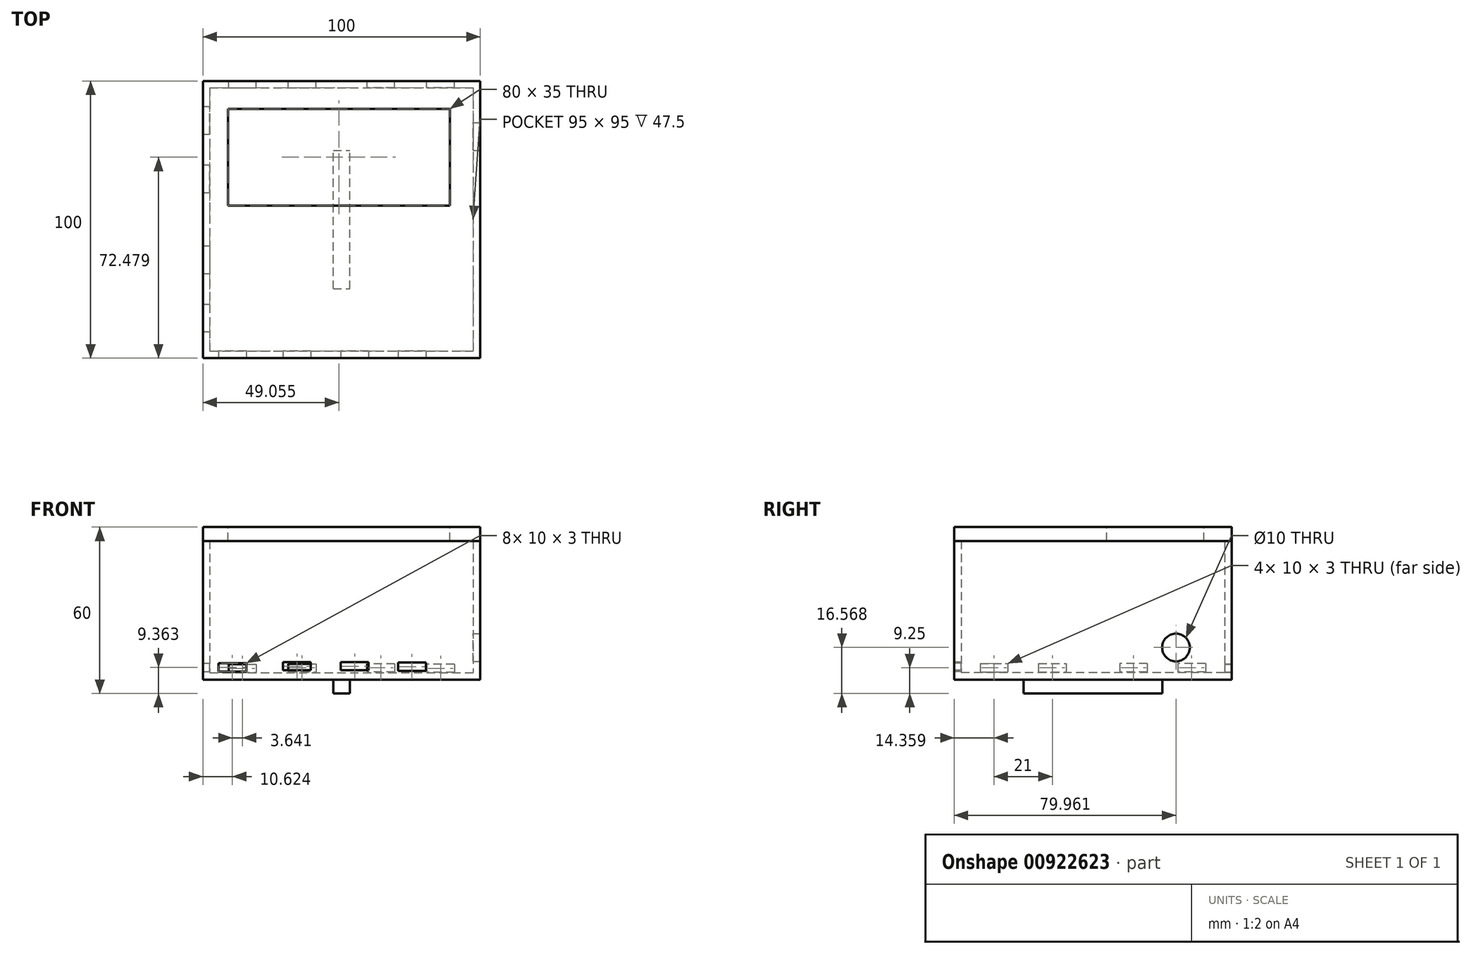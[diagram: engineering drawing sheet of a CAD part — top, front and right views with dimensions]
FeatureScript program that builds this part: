
annotation { "Feature Type Name" : "Feature", "Feature Type Description" : "" }
export const myFeature = defineFeature(function(context is Context, id is Id, definition is map)
    precondition{}
    {
        {
            var Q0;
            Q0=qCreatedBy(makeId("Top.planeOp"),FACE);
            var sketch = newSketch(context, id + "F0", { "sketchPlane" : qUnion([Q0])});
            skLineSegment(sketch, "E0.bottom", {"start": v(-50, 50) * mm, "end": v(50, 50) * mm});
            skLineSegment(sketch, "E0.top", {"start": v(-50, -50) * mm, "end": v(50, -50) * mm});
            skLineSegment(sketch, "E0.left", {"start": v(-50, 50) * mm, "end": v(-50, -50) * mm});
            skLineSegment(sketch, "E0.right", {"start": v(50, 50) * mm, "end": v(50, -50) * mm});
            skPoint(sketch, "E0.middle", {"position": v(0, 0) * mm});
            skSolve(sketch);
        }
        {
            var Q0;
            Q0=makeQuery(id+"F0.imprint","IMPRINT",FACE,{"disambiguationData":[TD([[makeQuery(id+"F0.imprint","IMPRINT",EDGE,{"derivedFrom":sQuery(id+"F0.wireOp",EDGE,"E0.bottom")}),-1.0]])]});
            extrude(context, id + "F1", {"entities" : qUnion([Q0]), "depth" : 50 * mm, "offsetDistance" : 25 * mm});
        }
        {
            var Q0;
            Q0=makeQuery(id+"F1.opExtrude","CAP_FACE",FACE,{"disambiguationData":[OSD([sQuery(id+"F0.wireOp",EDGE,"E0.bottom"),sQuery(id+"F0.wireOp",EDGE,"E0.top"),sQuery(id+"F0.wireOp",EDGE,"E0.left"),sQuery(id+"F0.wireOp",EDGE,"E0.right")])],"isStart":false});
            shell(context, id + "F2", {"entities" : qUnion([Q0]), "thickness" : 2.5 * mm});
        }
        {
            var Q0;
            Q0=makeQuery(id+"F1.opExtrude","SWEPT_FACE",FACE,{"disambiguationData":[OSD([sQuery(id+"F0.wireOp",EDGE,"E0.top")])]});
            var sketch = newSketch(context, id + "F3", { "sketchPlane" : qUnion([Q0])});
            skLineSegment(sketch, "E1.bottom", {"start": v(-44.38, 5.86) * mm, "end": v(-34.38, 5.86) * mm});
            skLineSegment(sketch, "E1.top", {"start": v(-44.38, 2.86) * mm, "end": v(-34.38, 2.86) * mm});
            skLineSegment(sketch, "E1.left", {"start": v(-44.38, 5.86) * mm, "end": v(-44.38, 2.86) * mm});
            skLineSegment(sketch, "E1.right", {"start": v(-34.38, 5.86) * mm, "end": v(-34.38, 2.86) * mm});
            skLineSegment(sketch, "E2.bottom", {"start": v(-21.08, 6.31) * mm, "end": v(-11.08, 6.31) * mm});
            skLineSegment(sketch, "E2.top", {"start": v(-21.08, 3.31) * mm, "end": v(-11.08, 3.31) * mm});
            skLineSegment(sketch, "E2.left", {"start": v(-21.08, 6.31) * mm, "end": v(-21.08, 3.31) * mm});
            skLineSegment(sketch, "E2.right", {"start": v(-11.08, 6.31) * mm, "end": v(-11.08, 3.31) * mm});
            skLineSegment(sketch, "E3.bottom", {"start": v(-0.26, 6.31) * mm, "end": v(9.74, 6.31) * mm});
            skLineSegment(sketch, "E3.top", {"start": v(-0.26, 3.31) * mm, "end": v(9.74, 3.31) * mm});
            skLineSegment(sketch, "E3.left", {"start": v(-0.26, 6.31) * mm, "end": v(-0.26, 3.31) * mm});
            skLineSegment(sketch, "E3.right", {"start": v(9.74, 6.31) * mm, "end": v(9.74, 3.31) * mm});
            skLineSegment(sketch, "E4.bottom", {"start": v(20.41, 6.15) * mm, "end": v(30.41, 6.15) * mm});
            skLineSegment(sketch, "E4.top", {"start": v(20.41, 3.15) * mm, "end": v(30.41, 3.15) * mm});
            skLineSegment(sketch, "E4.left", {"start": v(20.41, 6.15) * mm, "end": v(20.41, 3.15) * mm});
            skLineSegment(sketch, "E4.right", {"start": v(30.41, 6.15) * mm, "end": v(30.41, 3.15) * mm});
            skSolve(sketch);
        }
        {
            var Q0;
            Q0=makeQuery(id+"F3.imprint","IMPRINT",FACE,{"disambiguationData":[TD([[makeQuery(id+"F3.imprint","IMPRINT",EDGE,{"derivedFrom":sQuery(id+"F3.wireOp",EDGE,"E1.bottom")}),-1.0]])]});
            var Q1;
            Q1=makeQuery(id+"F3.imprint","IMPRINT",FACE,{"disambiguationData":[TD([[makeQuery(id+"F3.imprint","IMPRINT",EDGE,{"derivedFrom":sQuery(id+"F3.wireOp",EDGE,"E2.bottom")}),-1.0]])]});
            var Q2;
            Q2=makeQuery(id+"F3.imprint","IMPRINT",FACE,{"disambiguationData":[TD([[makeQuery(id+"F3.imprint","IMPRINT",EDGE,{"derivedFrom":sQuery(id+"F3.wireOp",EDGE,"E3.bottom")}),-1.0]])]});
            var Q3;
            Q3=makeQuery(id+"F3.imprint","IMPRINT",FACE,{"disambiguationData":[TD([[makeQuery(id+"F3.imprint","IMPRINT",EDGE,{"derivedFrom":sQuery(id+"F3.wireOp",EDGE,"E4.bottom")}),-1.0]])]});
            extrude(context, id + "F4", {"entities" : qUnion([Q0, Q1, Q2, Q3]), "operationType" : NewBodyOperationType.REMOVE, "oppositeDirection" : true, "depth" : 10 * mm, "offsetDistance" : 25 * mm});
        }
        {
            var Q0;
            Q0=makeQuery(id+"F1.opExtrude","SWEPT_FACE",FACE,{"disambiguationData":[OSD([sQuery(id+"F0.wireOp",EDGE,"E0.bottom")])]});
            var sketch = newSketch(context, id + "F5", { "sketchPlane" : qUnion([Q0])});
            skLineSegment(sketch, "E5.bottom", {"start": v(-40.74, 5.56) * mm, "end": v(-30.74, 5.56) * mm});
            skLineSegment(sketch, "E5.top", {"start": v(-40.74, 2.56) * mm, "end": v(-30.74, 2.56) * mm});
            skLineSegment(sketch, "E5.left", {"start": v(-40.74, 5.56) * mm, "end": v(-40.74, 2.56) * mm});
            skLineSegment(sketch, "E5.right", {"start": v(-30.74, 5.56) * mm, "end": v(-30.74, 2.56) * mm});
            skLineSegment(sketch, "E6.bottom", {"start": v(-19.2, 5.7) * mm, "end": v(-9.2, 5.7) * mm});
            skLineSegment(sketch, "E6.top", {"start": v(-19.2, 2.7) * mm, "end": v(-9.2, 2.7) * mm});
            skLineSegment(sketch, "E6.left", {"start": v(-19.2, 5.7) * mm, "end": v(-19.2, 2.7) * mm});
            skLineSegment(sketch, "E6.right", {"start": v(-9.2, 5.7) * mm, "end": v(-9.2, 2.7) * mm});
            skLineSegment(sketch, "E7.MirrorCS", {"start": v(40.74, 5.56) * mm, "end": v(30.74, 5.56) * mm});
            skLineSegment(sketch, "E8.MirrorCS", {"start": v(40.74, 5.56) * mm, "end": v(40.74, 2.56) * mm});
            skLineSegment(sketch, "E9.MirrorCS", {"start": v(40.74, 2.56) * mm, "end": v(30.74, 2.56) * mm});
            skLineSegment(sketch, "E10.MirrorCS", {"start": v(30.74, 5.56) * mm, "end": v(30.74, 2.56) * mm});
            skLineSegment(sketch, "E11.MirrorCS", {"start": v(19.2, 5.7) * mm, "end": v(19.2, 2.7) * mm});
            skLineSegment(sketch, "E12.MirrorCS", {"start": v(19.2, 5.7) * mm, "end": v(9.2, 5.7) * mm});
            skLineSegment(sketch, "E13.MirrorCS", {"start": v(9.2, 5.7) * mm, "end": v(9.2, 2.7) * mm});
            skLineSegment(sketch, "E14.MirrorCS", {"start": v(19.2, 2.7) * mm, "end": v(9.2, 2.7) * mm});
            skSolve(sketch);
        }
        {
            var Q0;
            Q0 = qSketchRegion(id + "F5", true);
            extrude(context, id + "F6", {"entities" : qUnion([Q0]), "operationType" : NewBodyOperationType.REMOVE, "oppositeDirection" : true, "depth" : 10 * mm, "offsetDistance" : 25 * mm});
        }
        {
            var Q0;
            Q0=makeQuery(id+"F1.opExtrude","SWEPT_FACE",FACE,{"disambiguationData":[OSD([sQuery(id+"F0.wireOp",EDGE,"E0.left")])]});
            var sketch = newSketch(context, id + "F7", { "sketchPlane" : qUnion([Q0])});
            skLineSegment(sketch, "E15.bottom", {"start": v(-40.64, 5.75) * mm, "end": v(-30.64, 5.75) * mm});
            skLineSegment(sketch, "E15.top", {"start": v(-40.64, 2.75) * mm, "end": v(-30.64, 2.75) * mm});
            skLineSegment(sketch, "E15.left", {"start": v(-40.64, 5.75) * mm, "end": v(-40.64, 2.75) * mm});
            skLineSegment(sketch, "E15.right", {"start": v(-30.64, 5.75) * mm, "end": v(-30.64, 2.75) * mm});
            skLineSegment(sketch, "E16.bottom", {"start": v(-19.64, 5.75) * mm, "end": v(-9.64, 5.75) * mm});
            skLineSegment(sketch, "E16.top", {"start": v(-19.64, 2.75) * mm, "end": v(-9.64, 2.75) * mm});
            skLineSegment(sketch, "E16.left", {"start": v(-19.64, 5.75) * mm, "end": v(-19.64, 2.75) * mm});
            skLineSegment(sketch, "E16.right", {"start": v(-9.64, 5.75) * mm, "end": v(-9.64, 2.75) * mm});
            skLineSegment(sketch, "E17.MirrorCS", {"start": v(40.64, 2.75) * mm, "end": v(30.64, 2.75) * mm});
            skLineSegment(sketch, "E18.MirrorCS", {"start": v(19.64, 2.75) * mm, "end": v(9.64, 2.75) * mm});
            skLineSegment(sketch, "E19.MirrorCS", {"start": v(40.64, 5.75) * mm, "end": v(40.64, 2.75) * mm});
            skLineSegment(sketch, "E20.MirrorCS", {"start": v(19.64, 5.75) * mm, "end": v(9.64, 5.75) * mm});
            skLineSegment(sketch, "E21.MirrorCS", {"start": v(19.64, 5.75) * mm, "end": v(19.64, 2.75) * mm});
            skLineSegment(sketch, "E22.MirrorCS", {"start": v(30.64, 5.75) * mm, "end": v(30.64, 2.75) * mm});
            skLineSegment(sketch, "E23.MirrorCS", {"start": v(40.64, 5.75) * mm, "end": v(30.64, 5.75) * mm});
            skLineSegment(sketch, "E24.MirrorCS", {"start": v(9.64, 5.75) * mm, "end": v(9.64, 2.75) * mm});
            skSolve(sketch);
        }
        {
            var Q0;
            Q0 = qSketchRegion(id + "F7", true);
            extrude(context, id + "F8", {"entities" : qUnion([Q0]), "operationType" : NewBodyOperationType.REMOVE, "oppositeDirection" : true, "depth" : 10 * mm, "offsetDistance" : 25 * mm});
        }
        {
            var Q0;
            Q0=makeQuery(id+"F1.opExtrude","SWEPT_FACE",FACE,{"disambiguationData":[OSD([sQuery(id+"F0.wireOp",EDGE,"E0.right")])]});
            var sketch = newSketch(context, id + "F9", { "sketchPlane" : qUnion([Q0])});
            skCircle(sketch, "E25", {"center": v(29.96, 11.57) * mm, "radius": 5 * mm});
            skSolve(sketch);
        }
        {
            var Q0;
            Q0 = qSketchRegion(id + "F9", true);
            extrude(context, id + "F10", {"entities" : qUnion([Q0]), "operationType" : NewBodyOperationType.REMOVE, "oppositeDirection" : true, "depth" : 10 * mm, "offsetDistance" : 25 * mm});
        }
        {
            var Q0;
            Q0=makeQuery(id+"F1.opExtrude","CAP_FACE",FACE,{"disambiguationData":[OSD([sQuery(id+"F0.wireOp",EDGE,"E0.bottom"),sQuery(id+"F0.wireOp",EDGE,"E0.top"),sQuery(id+"F0.wireOp",EDGE,"E0.left"),sQuery(id+"F0.wireOp",EDGE,"E0.right")])],"isStart":false});
            var sketch = newSketch(context, id + "F11", { "sketchPlane" : qUnion([Q0])});
            skLineSegment(sketch, "E26.bottom", {"start": v(-50, 50) * mm, "end": v(50, 50) * mm});
            skLineSegment(sketch, "E26.top", {"start": v(-50, -50) * mm, "end": v(50, -50) * mm});
            skLineSegment(sketch, "E26.left", {"start": v(-50, 50) * mm, "end": v(-50, -50) * mm});
            skLineSegment(sketch, "E26.right", {"start": v(50, 50) * mm, "end": v(50, -50) * mm});
            skSolve(sketch);
        }
        {
            var Q0;
            Q0 = qSketchRegion(id + "F11", true);
            extrude(context, id + "F12", {"entities" : qUnion([Q0]), "depth" : 5 * mm, "offsetDistance" : 25 * mm});
        }
        {
            var Q0;
            Q0=makeQuery(id+"F12.opExtrude","CAP_FACE",FACE,{"disambiguationData":[OSD([sQuery(id+"F11.wireOp",EDGE,"E26.bottom"),sQuery(id+"F11.wireOp",EDGE,"E26.top"),sQuery(id+"F11.wireOp",EDGE,"E26.left"),sQuery(id+"F11.wireOp",EDGE,"E26.right")])],"isStart":false});
            var sketch = newSketch(context, id + "F13", { "sketchPlane" : qUnion([Q0])});
            skLineSegment(sketch, "E27.bottom", {"start": v(-40.95, 39.98) * mm, "end": v(39.05, 39.98) * mm});
            skLineSegment(sketch, "E27.top", {"start": v(-40.95, 4.98) * mm, "end": v(39.05, 4.98) * mm});
            skLineSegment(sketch, "E27.left", {"start": v(-40.95, 39.98) * mm, "end": v(-40.95, 4.98) * mm});
            skLineSegment(sketch, "E27.right", {"start": v(39.05, 39.98) * mm, "end": v(39.05, 4.98) * mm});
            skSolve(sketch);
        }
        {
            var Q0;
            Q0 = qSketchRegion(id + "F13", true);
            extrude(context, id + "F14", {"entities" : qUnion([Q0]), "operationType" : NewBodyOperationType.REMOVE, "oppositeDirection" : true, "depth" : 5 * mm, "offsetDistance" : 25 * mm});
        }
        {
            var Q0;
            Q0=makeQuery(id+"F1.opExtrude","CAP_FACE",FACE,{"disambiguationData":[OSD([sQuery(id+"F0.wireOp",EDGE,"E0.bottom"),sQuery(id+"F0.wireOp",EDGE,"E0.top"),sQuery(id+"F0.wireOp",EDGE,"E0.left"),sQuery(id+"F0.wireOp",EDGE,"E0.right")])],"isStart":true});
            var sketch = newSketch(context, id + "F15", { "sketchPlane" : qUnion([Q0])});
            skLineSegment(sketch, "E28.bottom", {"start": v(-3, 25) * mm, "end": v(3, 25) * mm});
            skLineSegment(sketch, "E28.top", {"start": v(-3, -25) * mm, "end": v(3, -25) * mm});
            skLineSegment(sketch, "E28.left", {"start": v(-3, 25) * mm, "end": v(-3, -25) * mm});
            skLineSegment(sketch, "E28.right", {"start": v(3, 25) * mm, "end": v(3, -25) * mm});
            skPoint(sketch, "E28.middle", {"position": v(0, 0) * mm});
            skSolve(sketch);
        }
        {
            var Q0;
            Q0 = qSketchRegion(id + "F15", true);
            extrude(context, id + "F16", {"entities" : qUnion([Q0]), "operationType" : NewBodyOperationType.ADD, "depth" : 5 * mm, "offsetDistance" : 25 * mm});
        }
    });
